# Revit family: TY-B-TY4251_Imperial
name_source: partatom
category: Sprinklers
units: mm (PartAtom-declared; Revit-internal decimal feet)

## family parameters
Always vertical = Yes
Cut with Voids When Loaded = No
Maintain Annotation Orientation = No
OmniClass Number = 23.65.70.17.11.24
OmniClass Title = Fire Fighting Sprinkler Heads
Part Type = Normal
Room Calculation Point = No
Round Connector Dimension = Use Diameter
Shared = No
Work Plane-Based = No

## types (47) — shared parameters
COBie = Yes
COBie.Component.Name = Sprinklers:Pendent_SIN
COBie.Type = Yes
COBie.Type.AssetType = Fixed
COBie.Type.Category = Pr_70_55_97_84:Sprinklers
COBie.Type.Manufacturer = Tyco Fire Protection Products
COBie.Type.Material = Bronze
COBie.Type.Shape = Cylinder
COBie.Type.Size = 3/4"(DN20)
Coverage = Standard
Coverage_ = Standard
K-Factor = 114.87
Manufacturer = Tyco Fire Protection Products
Manufacturer URL = www.tyco-fire.com
Material_ = Bronze
Model = TY-B
Nominal Diameter 1 = 20 mm
Orifice = Extra Large
Orifice Size = 0 mm
Outside Diameter 1 = 27 mm
Response = Standard
Response_ = Standard
SIN No = TY4251
Takeout 1 = 59 mm
Technical Data Sheet No = TFP151
zero-valued in all types: COBie.Type.NominalHeight, COBie.Type.NominalLength, COBie.Type.NominalWidth, COBie.Type.ReplacementCost, Default Elevation, Style Id

## per-type parameters (varying)
| type | COBie.Component.Description | COBie.Type.Colour | COBie.Type.DurationUnit | COBie.Type.Finish | COBie.Type.ModelNumber | COBie.Type.ModelReference | COBie.Type.WarrantyGuarantorParts | Description | Finish_ | Part No | Temperature Rating |
| Pendent ¾" NPT 57°C Brass_57-591-1-135 | TY-B Wet Pendent  135°F K8.0 3/4 NPT Br | Yellow | year | Natural Brass | 57-591-1-135 | TY-B Wet Pendent  135°F K8.0 3/4 NPT Br | http://tycofsbp.com
TFPPTerms_of_Sale.pdf | TY-B Pendent Brass 57°C 8K ¾" NPT | Natural Brass | 57-591-1-135 | 57 °C |
| Pendent ¾" NPT 68°C Brass_57-591-1-155 | TY-B Wet Pendent  155°F K8.0 3/4 NPT Br | Yellow | year | Natural Brass | 57-591-1-155 | TY-B Wet Pendent  155°F K8.0 3/4 NPT Br | http://tycofsbp.com
TFPPTerms_of_Sale.pdf | TY-B Pendent Brass 68°C 8K ¾" NPT | Natural Brass | 57-591-1-155 | 68 °C |
| Pendent ¾" NPT 79°C Brass_57-591-1-175 | TY-B Wet Pendent  175°F K8.0 3/4 NPT Br | Yellow | year | Natural Brass | 57-591-1-175 | TY-B Wet Pendent  175°F K8.0 3/4 NPT Br | http://tycofsbp.com
TFPPTerms_of_Sale.pdf | TY-B Pendent Brass 79°C 8K ¾" NPT | Natural Brass | 57-591-1-175 | 79 °C |
| Pendent ¾" NPT 93°C Brass_57-591-1-200 | TY-B Wet Pendent  200°F K8.0 3/4 NPT Br | Yellow | year | Natural Brass | 57-591-1-200 | TY-B Wet Pendent  200°F K8.0 3/4 NPT Br | http://tycofsbp.com
TFPPTerms_of_Sale.pdf | TY-B Pendent Brass 93°C 8K ¾" NPT | Natural Brass | 57-591-1-200 | 93 °C |
| Pendent ¾" NPT 141°C Brass_57-591-1-286 | TY-B Wet Pendent  286°F K8.0 3/4 NPT Br | Yellow | year | Natural Brass | 57-591-1-286 | TY-B Wet Pendent  286°F K8.0 3/4 NPT Br | http://tycofsbp.com
TFPPTerms_of_Sale.pdf | TY-B Pendent Brass 141°C 8K ¾" NPT | Natural Brass | 57-591-1-286 | 141 °C |
| Pendent ¾" NPT 182°C Brass_57-591-1-360 | TY-B Wet Pendent  360°F K8.0 3/4 NPT Br | Yellow | year | Natural Brass | 57-591-1-360 | TY-B Wet Pendent  360°F K8.0 3/4 NPT Br | http://tycofsbp.com
TFPPTerms_of_Sale.pdf | TY-B Pendent Brass 182°C 8K ¾" NPT | Natural Brass | 57-591-1-360 | 182 °C |
| Pendent ¾" NPT 57°C Poly-Stainless Grey Aluminium_57-591-2-135 | TY-B Wet Pendent  135°F K8.0 3/4 NPT RAL9007 | Gray | year | Poly-Stainless Gray | 57-591-2-135 | TY-B Wet Pendent  135°F K8.0 3/4 NPT RAL9007 | http://tycofsbp.com
TFPPTerms_of_Sale.pdf | TY-B Pendent Brass 57°C 8K ¾" NPT | Poly-Stainless Grey Aluminium Polyester (RAL9007) | 57-591-2-135 | 57 °C |
| Pendent ¾" NPT 68°C Poly-Stainless Grey Aluminium_57-591-2-155 | TY-B Wet Pendent  155°F K8.0 3/4 NPT RAL9007 | Gray | year | Poly-Stainless Gray | 57-591-2-155 | TY-B Wet Pendent  155°F K8.0 3/4 NPT RAL9007 | http://tycofsbp.com
TFPPTerms_of_Sale.pdf | TY-B Pendent Brass 68°C 8K ¾" NPT | Poly-Stainless Grey Aluminium Polyester (RAL9007) | 57-591-2-155 | 68 °C |
| Pendent ¾" NPT 79°C Poly-Stainless Grey Aluminium_57-591-2-175 | TY-B Wet Pendent  175°F K8.0 3/4 NPT RAL9007 | Gray | year | Poly-Stainless Gray | 57-591-2-175 | TY-B Wet Pendent  175°F K8.0 3/4 NPT RAL9007 | http://tycofsbp.com
TFPPTerms_of_Sale.pdf | TY-B Pendent Brass 79°C 8K ¾" NPT | Poly-Stainless Grey Aluminium Polyester (RAL9007) | 57-591-2-175 | 79 °C |
| Pendent ¾" NPT 93°C Poly-Stainless Grey Aluminium_57-591-2-200 | TY-B Wet Pendent  200°F K8.0 3/4 NPT RAL9007 | Gray | year | Poly-Stainless Gray | 57-591-2-200 | TY-B Wet Pendent  200°F K8.0 3/4 NPT RAL9007 | http://tycofsbp.com
TFPPTerms_of_Sale.pdf | TY-B Pendent Brass 93°C 8K ¾" NPT | Poly-Stainless Grey Aluminium Polyester (RAL9007) | 57-591-2-200 | 93 °C |
| Pendent ¾" NPT 141°C Poly-Stainless Grey Aluminium_57-591-2-286 | TY-B Wet Pendent  286°F K8.0 3/4 NPT RAL9007 | Gray | year | Poly-Stainless Gray | 57-591-2-286 | TY-B Wet Pendent  286°F K8.0 3/4 NPT RAL9007 | http://tycofsbp.com
TFPPTerms_of_Sale.pdf | TY-B Pendent Brass 141°C 8K ¾" NPT | Poly-Stainless Grey Aluminium Polyester (RAL9007) | 57-591-2-286 | 141 °C |
| Pendent ¾" NPT 182°C Poly-Stainless Grey Aluminium_57-591-2-360 | TY-B Wet Pendent  360°F K8.0 3/4 NPT RAL9007 | Gray | year | Poly-Stainless Gray | 57-591-2-360 | TY-B Wet Pendent  360°F K8.0 3/4 NPT RAL9007 | http://tycofsbp.com
TFPPTerms_of_Sale.pdf | TY-B Pendent Brass 182°C 8K ¾" NPT | Poly-Stainless Grey Aluminium Polyester (RAL9007) | 57-591-2-360 | 182 °C |
| Pendent ¾" NPT 57°C White_57-591-3-135 | TY-B Wet Pendent  135°F K8.0 3/4 NPT Wh9010 | White | year | Pure White | 57-591-3-135 | TY-B Wet Pendent  135°F K8.0 3/4 NPT Wh9010 | http://tycofsbp.com
TFPPTerms_of_Sale.pdf | TY-B Pendent White 57°C 8K ¾" NPT | White RAL9010 | 57-591-3-135 | 57 °C |
| Pendent ¾" NPT 68°C White_57-591-3-155 | TY-B Wet Pendent  155°F K8.0 3/4 NPT Wh9010 | White | year | Pure White | 57-591-3-155 | TY-B Wet Pendent  155°F K8.0 3/4 NPT Wh9010 | http://tycofsbp.com
TFPPTerms_of_Sale.pdf | TY-B Pendent White 68°C 8K ¾" NPT | White RAL9010 | 57-591-3-155 | 68 °C |
| Pendent ¾" NPT 79°C White_57-591-3-175 | TY-B Wet Pendent  175°F K8.0 3/4 NPT Wh9010 | White | year | Pure White | 57-591-3-175 | TY-B Wet Pendent  175°F K8.0 3/4 NPT Wh9010 | http://tycofsbp.com
TFPPTerms_of_Sale.pdf | TY-B Pendent White 79°C 8K ¾" NPT | White RAL9010 | 57-591-3-175 | 79 °C |
| Pendent ¾" NPT 93°C White_57-591-3-200 | TY-B Wet Pendent  200°F K8.0 3/4 NPT Wh9010 | White | year | Pure White | 57-591-3-200 | TY-B Wet Pendent  200°F K8.0 3/4 NPT Wh9010 | http://tycofsbp.com
TFPPTerms_of_Sale.pdf | TY-B Pendent White 93°C 8K ¾" NPT | White RAL9010 | 57-591-3-200 | 93 °C |
| Pendent ¾" NPT 141°C White_57-591-3-286 | TY-B Wet Pendent  286°F K8.0 3/4 NPT Wh9010 | White | year | Pure White | 57-591-3-286 | TY-B Wet Pendent  286°F K8.0 3/4 NPT Wh9010 | http://tycofsbp.com
TFPPTerms_of_Sale.pdf | TY-B Pendent White 141°C 8K ¾" NPT | White RAL9010 | 57-591-3-286 | 141 °C |
| Pendent ¾" NPT 182°C White_57-591-3-360 | TY-B Wet Pendent  360°F K8.0 3/4 NPT Wh9010 | White | year | Pure White | 57-591-3-360 | TY-B Wet Pendent  360°F K8.0 3/4 NPT Wh9010 | http://tycofsbp.com
TFPPTerms_of_Sale.pdf | TY-B Pendent White 182°C 8K ¾" NPT | White RAL9010 | 57-591-3-360 | 182 °C |
| Pendent ¾" NPT 57°C White_57-591-4-135 | TY-B Wet Pendent  57.2°C K115 DN20 NPT Wh9003 | White | year | Signal White | 57-591-4-135 | TY-B Wet Pendent  57.2°C K115 DN20 NPT Wh9003 | http://tycofsbp.com | TY-B Pendent White 57°C 8K ¾" NPT | White RAL9003 | 57-591-4-135 | 57 °C |
| Pendent ¾" NPT 68°C White_57-591-4-155 | TY-B Wet Pendent  68.3°C K115 DN20 NPT Wh9003 | White | year | Signal White | 57-591-4-155 | TY-B Wet Pendent  68.3°C K115 DN20 NPT Wh9003 | http://tycofsbp.com | TY-B Pendent White 68°C 8K ¾" NPT | White RAL9003 | 57-591-4-155 | 68 °C |
| Pendent ¾" NPT 79°C White_57-591-4-175 | TY-B Wet Pendent  79.4°C K115 DN20 NPT Wh9003 | White | year | Signal White | 57-591-4-175 | TY-B Wet Pendent  79.4°C K115 DN20 NPT Wh9003 | http://tycofsbp.com | TY-B Pendent White 79°C 8K ¾" NPT | White RAL9003 | 57-591-4-175 | 79 °C |
| Pendent ¾" NPT 93°C White_57-591-4-200 | TY-B Wet Pendent  93.3°C K115 DN20 NPT Wh9003 | White | year | Signal White | 57-591-4-200 | TY-B Wet Pendent  93.3°C K115 DN20 NPT Wh9003 | http://tycofsbp.com | TY-B Pendent White 93°C 8K ¾" NPT | White RAL9003 | 57-591-4-200 | 93 °C |
| Pendent ¾" NPT 141°C White_57-591-4-286 | TY-B Wet Pendent  141.1°C K115 DN20 NPT Wh9003 | White | year | Signal White | 57-591-4-286 | TY-B Wet Pendent  141.1°C K115 DN20 NPT Wh9003 | http://tycofsbp.com | TY-B Pendent White 141°C 8K ¾" NPT | White RAL9003 | 57-591-4-286 | 141 °C |
| Pendent ¾" NPT 182°C White_57-591-4-360 | TY-B Wet Pendent  182.2°C K115 DN20 NPT Wh9003 | White | year | Signal White | 57-591-4-360 | TY-B Wet Pendent  182.2°C K115 DN20 NPT Wh9003 | http://tycofsbp.com | TY-B Pendent White 182°C 8K ¾" NPT | White RAL9003 | 57-591-4-360 | 182 °C |
| Pendent ¾" NPT 68°C JetBlack_57-591-5-155 | TY-B Wet Pendent  68.3°C K115 DN20 NPT JBlk | Black | year | Jet Black | 57-591-5-155 | TY-B Wet Pendent  68.3°C K115 DN20 NPT JBlk | http://tycofsbp.com | TY-B Pendent JetBlack 68°C 8K ¾" NPT | Jet Black RAL9005 | 57-591-5-155 | 68 °C |
| Pendent ¾" NPT 93°C JetBlack_57-591-5-200 | TY-B Wet Pendent  93.3°C K115 DN20 NPT JBlk | Black | year | Jet Black | 57-591-5-200 | TY-B Wet Pendent  93.3°C K115 DN20 NPT JBlk | http://tycofsbp.com | TY-B Pendent JetBlack 93°C 8K ¾" NPT | Jet Black RAL9005 | 57-591-5-200 | 93 °C |
| Pendent ¾" NPT 57°C Wax_57-591-6-135 | TY-B Wet Pendent  135°F K8.0 3/4 NPT Wx | Gray | year | Wax Coated | 57-591-6-135 | TY-B Wet Pendent  135°F K8.0 3/4 NPT Wx | http://tycofsbp.com
TFPPTerms_of_Sale.pdf | TY-B Pendent Wax 57°C 8K ¾" NPT | Wax Coated | 57-591-6-135 | 57 °C |
| Pendent ¾" NPT 68°C Wax_57-591-6-155 | TY-B Wet Pendent  155°F K8.0 3/4 NPT Wx | Gray | year | Wax Coated | 57-591-6-155 | TY-B Wet Pendent  155°F K8.0 3/4 NPT Wx | http://tycofsbp.com
TFPPTerms_of_Sale.pdf | TY-B Pendent Wax 68°C 8K ¾" NPT | Wax Coated | 57-591-6-155 | 68 °C |
| Pendent ¾" NPT 79°C Wax_57-591-6-175 | TY-B Wet Pendent  175°F K8.0 3/4 NPT Wx | Gray | year | Wax Coated | 57-591-6-175 | TY-B Wet Pendent  175°F K8.0 3/4 NPT Wx | http://tycofsbp.com
TFPPTerms_of_Sale.pdf | TY-B Pendent Wax 79°C 8K ¾" NPT | Wax Coated | 57-591-6-175 | 79 °C |
| Pendent ¾" NPT 141°C Wax_57-591-6-286 | TY-B Wet Pendent  286°F K8.0 3/4 NPT Wx | Gray | year | Wax Coated | 57-591-6-286 | TY-B Wet Pendent  286°F K8.0 3/4 NPT Wx | http://tycofsbp.com
TFPPTerms_of_Sale.pdf | TY-B Pendent Wax 141°C 8K ¾" NPT | Wax Coated | 57-591-6-286 | 141 °C |
| Pendent ¾" NPT 57°C Lead_57-591-7-135 | TY-B Wet Pendent  135°F K8.0 3/4 NPT Lead | Gray | year | Lead Coated | 57-591-7-135 | TY-B Wet Pendent  135°F K8.0 3/4 NPT Lead | http://tycofsbp.com
TFPPTerms_of_Sale.pdf | TY-B Pendent Lead 57°C 8K ¾" NPT | Lead Coated | 57-591-7-135 | 57 °C |
| Pendent ¾" NPT 68°C Lead_57-591-7-155 | TY-B Wet Pendent  155°F K8.0 3/4 NPT Lead | Gray | year | Lead Coated | 57-591-7-155 | TY-B Wet Pendent  155°F K8.0 3/4 NPT Lead | http://tycofsbp.com
TFPPTerms_of_Sale.pdf | TY-B Pendent Lead 68°C 8K ¾" NPT | Lead Coated | 57-591-7-155 | 68 °C |
| Pendent ¾" NPT 79°C Lead_57-591-7-175 | TY-B Wet Pendent  175°F K8.0 3/4 NPT Lead | Gray | year | Lead Coated | 57-591-7-175 | TY-B Wet Pendent  175°F K8.0 3/4 NPT Lead | http://tycofsbp.com
TFPPTerms_of_Sale.pdf | TY-B Pendent Lead 79°C 8K ¾" NPT | Lead Coated | 57-591-7-175 | 79 °C |
| Pendent ¾" NPT 93°C Lead_57-591-7-200 | TY-B Wet Pendent  200°F K8.0 3/4 NPT Lead | Gray | year | Lead Coated | 57-591-7-200 | TY-B Wet Pendent  200°F K8.0 3/4 NPT Lead | http://tycofsbp.com
TFPPTerms_of_Sale.pdf | TY-B Pendent Lead 93°C 8K ¾" NPT | Lead Coated | 57-591-7-200 | 93 °C |
| Pendent ¾" NPT 141°C Lead_57-591-7-286 | TY-B Wet Pendent  286°F K8.0 3/4 NPT Lead | Gray | year | Lead Coated | 57-591-7-286 | TY-B Wet Pendent  286°F K8.0 3/4 NPT Lead | http://tycofsbp.com
TFPPTerms_of_Sale.pdf | TY-B Pendent Lead 141°C 8K ¾" NPT | Lead Coated | 57-591-7-286 | 141 °C |
| Pendent ¾" NPT 182°C Lead_57-591-7-360 | TY-B Wet Pendent  360°F K8.0 3/4 NPT Lead | Gray | Year | Lead Coated | 57-591-7-360 | TY-B Wet Pendent  360°F K8.0 3/4 NPT Lead | http://tycofsbp.com
TFPPTerms_of_Sale.pdf | TY-B Pendent Lead 182°C 8K ¾" NPT | Lead Coated | 57-591-7-360 | 182 °C |
| Pendent ¾" NPT 57°C Wax Over Lead_57-591-8-135 | TY-B Wet Pendent  135°F K8.0 3/4 NPT WoL | Gray | year | Wax-Over-Lead | 57-591-8-135 | TY-B Wet Pendent  135°F K8.0 3/4 NPT WoL | http://tycofsbp.com
TFPPTerms_of_Sale.pdf | TY-B Pendent Wax Over Lead 57°C 8K ¾" NPT | Wax Over Lead | 57-591-8-135 | 57 °C |
| Pendent ¾" NPT 68°C Wax Over Lead_57-591-8-155 | TY-B Wet Pendent  155°F K8.0 3/4 NPT WoL | Gray | year | Wax-Over-Lead | 57-591-8-155 | TY-B Wet Pendent  155°F K8.0 3/4 NPT WoL | http://tycofsbp.com
TFPPTerms_of_Sale.pdf | TY-B Pendent Wax Over Lead 68°C 8K ¾" NPT | Wax Over Lead | 57-591-8-155 | 68 °C |
| Pendent ¾" NPT 79°C Wax Over Lead_57-591-8-175 | TY-B Wet Pendent  175°F K8.0 3/4 NPT WoL | Gray | year | Wax-Over-Lead | 57-591-8-175 | TY-B Wet Pendent  175°F K8.0 3/4 NPT WoL | http://tycofsbp.com
TFPPTerms_of_Sale.pdf | TY-B Pendent Wax Over Lead 79°C 8K ¾" NPT | Wax Over Lead | 57-591-8-175 | 79 °C |
| Pendent ¾" NPT 93°C Wax Over Lead_57-591-8-200 | TY-B Wet Pendent  200°F K8.0 3/4 NPT WoL | Gray | year | Wax-Over-Lead | 57-591-8-200 | TY-B Wet Pendent  200°F K8.0 3/4 NPT WoL | http://tycofsbp.com
TFPPTerms_of_Sale.pdf | TY-B Pendent Wax Over Lead 93°C 8K ¾" NPT | Wax Over Lead | 57-591-8-200 | 93 °C |
| Pendent ¾" NPT 141°C Wax Over Lead_57-591-8-286 | TY-B Wet Pendent  286°F K8.0 3/4 NPT WoL | Gray | year | Wax-Over-Lead | 57-591-8-286 | TY-B Wet Pendent  286°F K8.0 3/4 NPT WoL | http://tycofsbp.com
TFPPTerms_of_Sale.pdf | TY-B Pendent Wax Over Lead 141°C 8K ¾" NPT | Wax Over Lead | 57-591-8-286 | 141 °C |
| Pendent ¾" NPT 57°C Chrome_57-591-9-135 | TY-B Wet Pendent  135°F K8.0 3/4 NPT Chr | Silver | year | Chrome Plated | 57-591-9-135 | TY-B Wet Pendent  135°F K8.0 3/4 NPT Chr | http://tycofsbp.com
TFPPTerms_of_Sale.pdf | TY-B Pendent Chrome 57°C 8K ¾" NPT | Chrome Plated | 57-591-9-135 | 57 °C |
| Pendent ¾" NPT 68°C Chrome_57-591-9-155 | TY-B Wet Pendent  155°F K8.0 3/4 NPT Chr | Silver | year | Chrome Plated | 57-591-9-155 | TY-B Wet Pendent  155°F K8.0 3/4 NPT Chr | http://tycofsbp.com
TFPPTerms_of_Sale.pdf | TY-B Pendent Chrome 68°C 8K ¾" NPT | Chrome Plated | 57-591-9-155 | 68 °C |
| Pendent ¾" NPT 79°C Chrome_57-591-9-175 | TY-B Wet Pendent  175°F K8.0 3/4 NPT Chr | Silver | year | Chrome Plated | 57-591-9-175 | TY-B Wet Pendent  175°F K8.0 3/4 NPT Chr | http://tycofsbp.com
TFPPTerms_of_Sale.pdf | TY-B Pendent Chrome 79°C 8K ¾" NPT | Chrome Plated | 57-591-9-175 | 79 °C |
| Pendent ¾" NPT 93°C Chrome_57-591-9-200 | TY-B Wet Pendent  200°F K8.0 3/4 NPT Chr | Silver | year | Chrome Plated | 57-591-9-200 | TY-B Wet Pendent  200°F K8.0 3/4 NPT Chr | http://tycofsbp.com
TFPPTerms_of_Sale.pdf | TY-B Pendent Chrome 93°C 8K ¾" NPT | Chrome Plated | 57-591-9-200 | 93 °C |
| Pendent ¾" NPT 141°C Chrome_57-591-9-286 | TY-B Wet Pendent  286°F K8.0 3/4 NPT Chr | Silver | year | Chrome Plated | 57-591-9-286 | TY-B Wet Pendent  286°F K8.0 3/4 NPT Chr | http://tycofsbp.com
TFPPTerms_of_Sale.pdf | TY-B Pendent Chrome 141°C 8K ¾" NPT | Chrome Plated | 57-591-9-286 | 141 °C |
| Pendent ¾" NPT 182°C Chrome_57-591-9-360 | TY-B Wet Pendent  360°F K8.0 3/4 NPT Chr | Silver | year | Chrome Plated | 57-591-9-360 | TY-B Wet Pendent  360°F K8.0 3/4 NPT Chr | http://tycofsbp.com
TFPPTerms_of_Sale.pdf | TY-B Pendent Chrome 182°C 8K ¾" NPT | Chrome Plated | 57-591-9-360 | 182 °C |

## geometry (parser evidence)
native form markers: Blend x2, Sweep x53
no freeform markers — native parametric forms only
